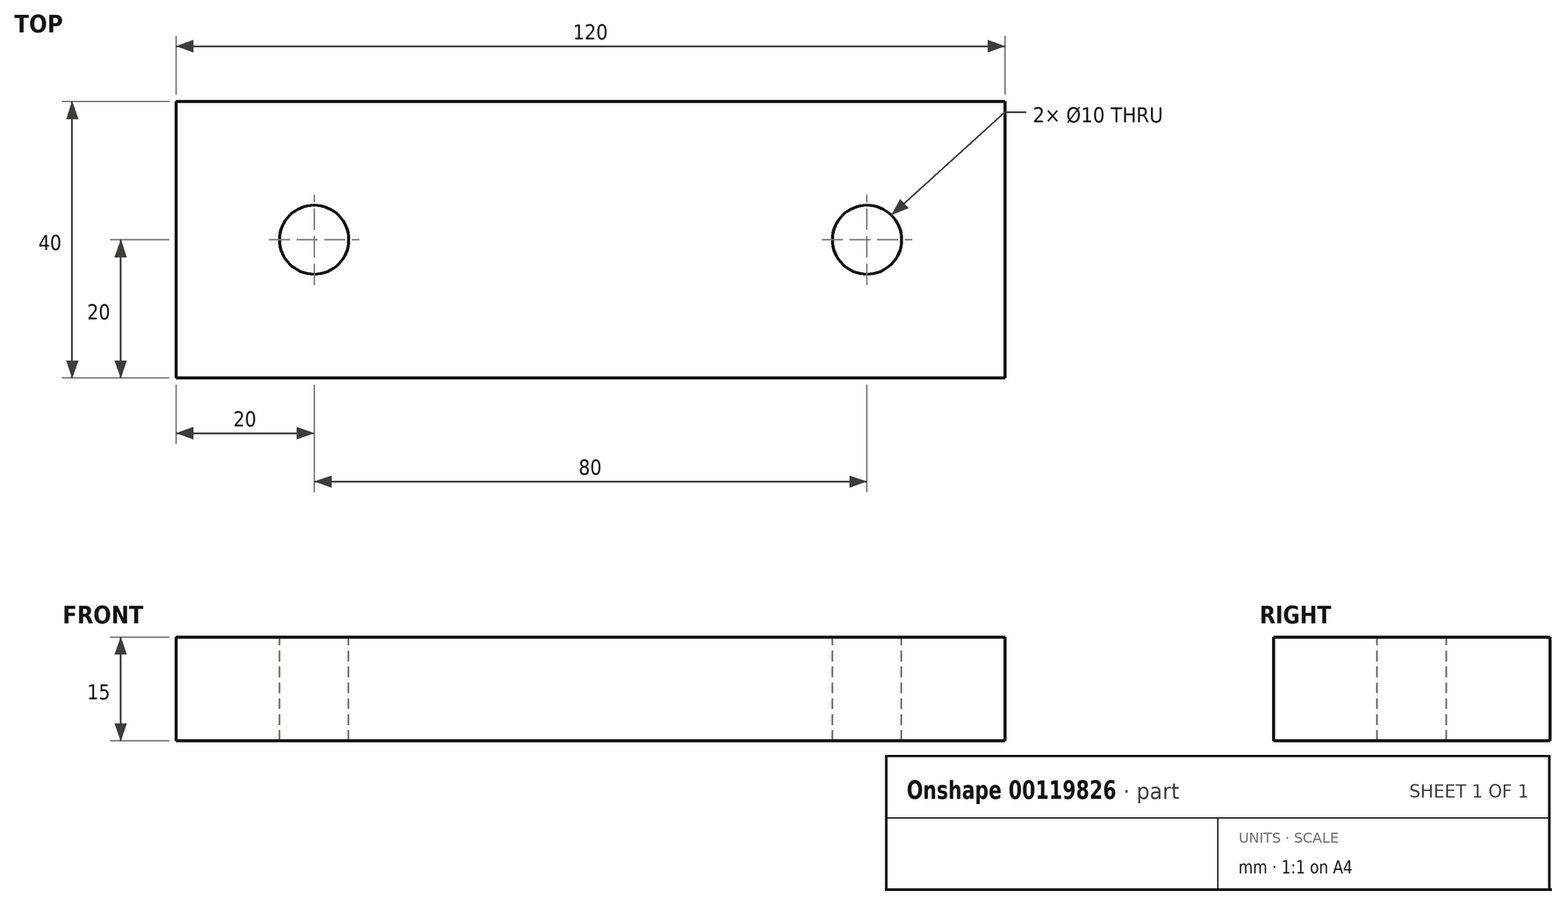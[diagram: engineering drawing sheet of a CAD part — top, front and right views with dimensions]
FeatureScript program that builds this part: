
annotation { "Feature Type Name" : "Feature", "Feature Type Description" : "" }
export const myFeature = defineFeature(function(context is Context, id is Id, definition is map)
    precondition{}
    {
        {
            var Q0;
            Q0=qCreatedBy(makeId("Top.planeOp"),FACE);
            var sketch = newSketch(context, id + "F0", { "sketchPlane" : qUnion([Q0])});
            skLineSegment(sketch, "E0", {"start": v(0, 0) * mm, "end": v(0, 40) * mm});
            skLineSegment(sketch, "E1", {"start": v(0, 40) * mm, "end": v(120, 40) * mm});
            skLineSegment(sketch, "E2", {"start": v(120, 40) * mm, "end": v(120, 0) * mm});
            skLineSegment(sketch, "E3", {"start": v(120, 0) * mm, "end": v(0, 0) * mm});
            skSolve(sketch);
        }
        {
            var Q0;
            Q0 = qSketchRegion(id + "F0", true);
            extrude(context, id + "F1", {"entities" : qUnion([Q0]), "oppositeDirection" : true, "depth" : 15 * mm});
        }
        {
            var Q0;
            Q0=qCreatedBy(makeId("Top.planeOp"),FACE);
            var sketch = newSketch(context, id + "F2", { "sketchPlane" : qUnion([Q0])});
            skCircle(sketch, "E4", {"center": v(20, 20) * mm, "radius": 5 * mm});
            skCircle(sketch, "E5", {"center": v(100, 20) * mm, "radius": 5 * mm});
            skSolve(sketch);
        }
        {
            var Q0;
            Q0=makeQuery(id+"F2.imprint","IMPRINT",FACE,{"disambiguationData":[TD([[makeQuery(id+"F2.imprint","IMPRINT",EDGE,{"derivedFrom":sQuery(id+"F2.wireOp",EDGE,"E4")}),1.0]])]});
            var Q1;
            Q1=makeQuery(id+"F2.imprint","IMPRINT",FACE,{"disambiguationData":[TD([[makeQuery(id+"F2.imprint","IMPRINT",EDGE,{"derivedFrom":sQuery(id+"F2.wireOp",EDGE,"E5")}),1.0]])]});
            extrude(context, id + "F3", {"entities" : qUnion([Q0, Q1]), "operationType" : NewBodyOperationType.REMOVE, "endBound" : BoundingType.THROUGH_ALL, "oppositeDirection" : true, "depth" : 25 * mm});
        }
    });
